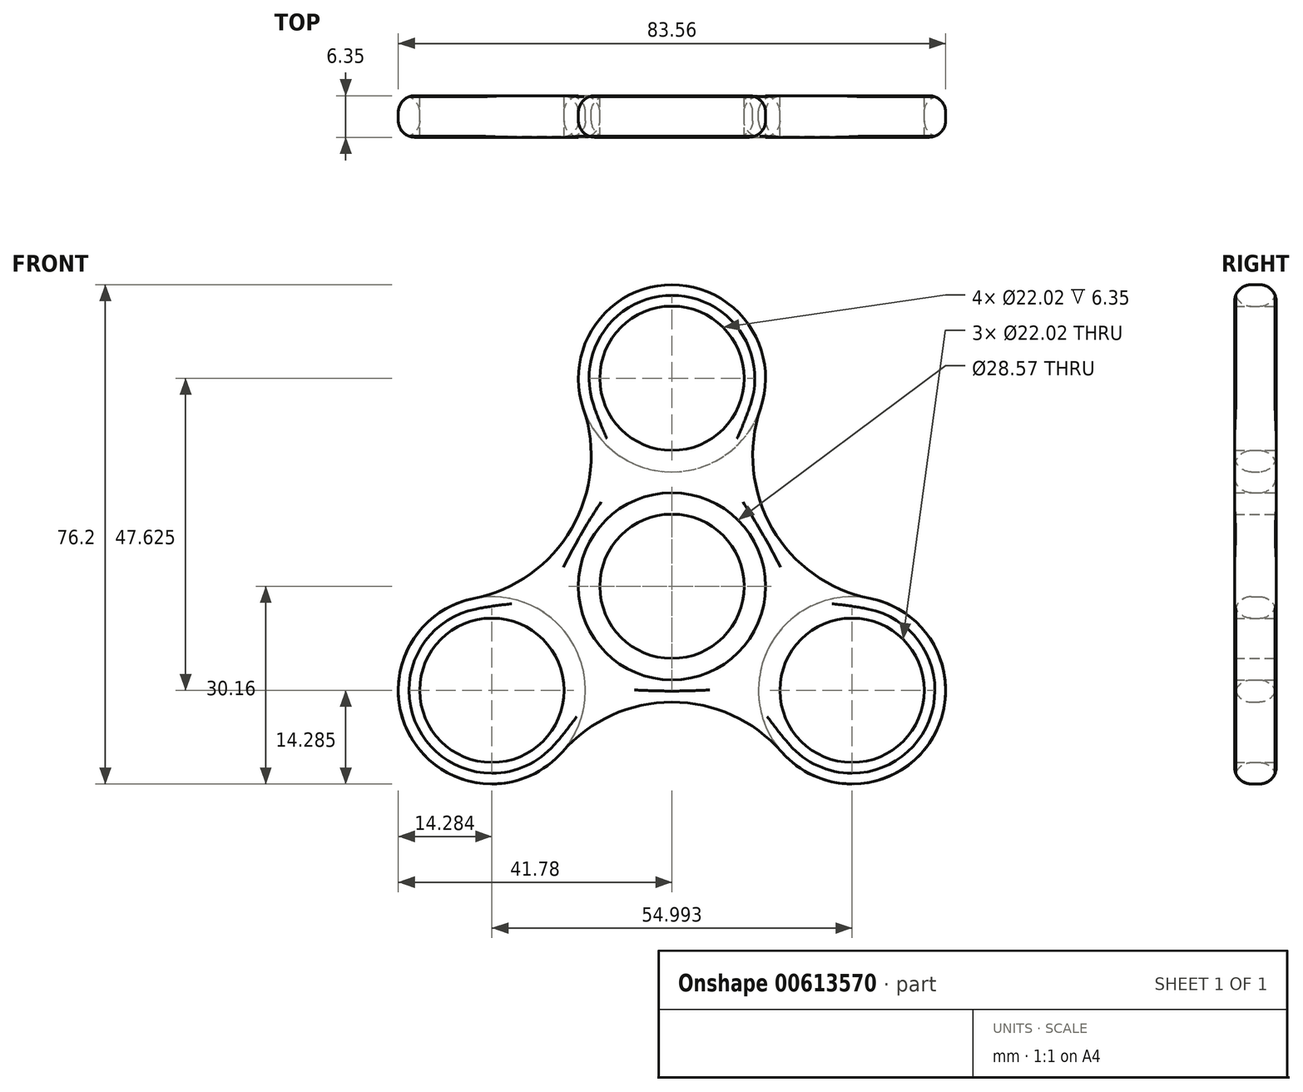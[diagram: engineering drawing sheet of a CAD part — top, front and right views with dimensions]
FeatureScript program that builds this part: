
annotation { "Feature Type Name" : "Feature", "Feature Type Description" : "" }
export const myFeature = defineFeature(function(context is Context, id is Id, definition is map)
    precondition{}
    {
        {
            var Q0;
            Q0=qCreatedBy(makeId("Front.planeOp"),FACE);
            var sketch = newSketch(context, id + "F0", { "sketchPlane" : qUnion([Q0])});
            skCircle(sketch, "E0", {"center": v(0, 0) * mm, "radius": 14.29 * mm});
            skCircle(sketch, "E1", {"center": v(0, 0) * mm, "radius": 11.01 * mm});
            skCircle(sketch, "E2", {"center": v(0, 31.75) * mm, "radius": 14.29 * mm});
            skCircle(sketch, "E3", {"center": v(0, 31.75) * mm, "radius": 11.01 * mm});
            skCircle(sketch, "E4.1.0", {"center": v(-27.5, -15.87) * mm, "radius": 11.01 * mm});
            skCircle(sketch, "E4.1.1", {"center": v(-27.5, -15.87) * mm, "radius": 14.29 * mm});
            skCircle(sketch, "E4.2.0", {"center": v(27.5, -15.88) * mm, "radius": 11.01 * mm});
            skCircle(sketch, "E4.2.1", {"center": v(27.5, -15.88) * mm, "radius": 14.29 * mm});
            skSolve(sketch);
        }
        {
            var Q0;
            Q0=makeQuery(id+"F0.imprint","IMPRINT",FACE,{"disambiguationData":[TD([[makeQuery(id+"F0.imprint","IMPRINT",EDGE,{"derivedFrom":sQuery(id+"F0.wireOp",EDGE,"E3")}),1.0]])]});
            var sketch = newSketch(context, id + "F1", { "sketchPlane" : qUnion([Q0])});
            skCircle(sketch, "E5.0", {"center": v(0, 31.75) * mm, "radius": 14.29 * mm});
            skCircle(sketch, "E6.0", {"center": v(-27.5, -15.87) * mm, "radius": 14.29 * mm});
            skCircle(sketch, "E7.0", {"center": v(0, 0) * mm, "radius": 14.29 * mm});
            skCircle(sketch, "E8.0", {"center": v(27.5, -15.88) * mm, "radius": 14.29 * mm});
            skArc(sketch, "E9", {"start": v(-30.26, -1.86) * mm, "mid": v(-15.3, 8.84) * mm, "end": v(-13.52, 27.13) * mm});
            skArc(sketch, "E10", {"start": v(13.52, 27.13) * mm, "mid": v(15.3, 8.84) * mm, "end": v(30.26, -1.86) * mm});
            skArc(sketch, "E11", {"start": v(16.74, -25.28) * mm, "mid": v(0, -17.67) * mm, "end": v(-16.74, -25.28) * mm});
            skCircle(sketch, "E12", {"center": v(0, 0) * mm, "radius": 11.01 * mm});
            skCircle(sketch, "E13", {"center": v(27.5, -15.88) * mm, "radius": 11.01 * mm});
            skCircle(sketch, "E14", {"center": v(-27.5, -15.87) * mm, "radius": 11.01 * mm});
            skCircle(sketch, "E15", {"center": v(0, 31.75) * mm, "radius": 11.01 * mm});
            skSolve(sketch);
        }
        {
            var Q0;
            Q0=makeQuery(id+"F0.imprint","IMPRINT",FACE,{"disambiguationData":[TD([[makeQuery(id+"F0.imprint","IMPRINT",EDGE,{"derivedFrom":sQuery(id+"F0.wireOp",EDGE,"E2")}),1.0]])]});
            var Q1;
            Q1=makeQuery(id+"F0.imprint","IMPRINT",FACE,{"disambiguationData":[TD([[makeQuery(id+"F0.imprint","IMPRINT",EDGE,{"derivedFrom":sQuery(id+"F0.wireOp",EDGE,"E0")}),1.0]])]});
            var Q2;
            Q2 = qSketchRegion(id + "F1", true);
            var Q3;
            Q3=makeQuery(id+"F0.imprint","IMPRINT",FACE,{"disambiguationData":[TD([[makeQuery(id+"F0.imprint","IMPRINT",EDGE,{"derivedFrom":sQuery(id+"F0.wireOp",EDGE,"E4.1.0")}),-1.0]])]});
            var Q4;
            Q4=makeQuery(id+"F0.imprint","IMPRINT",FACE,{"disambiguationData":[TD([[makeQuery(id+"F0.imprint","IMPRINT",EDGE,{"derivedFrom":sQuery(id+"F0.wireOp",EDGE,"E4.2.0")}),-1.0]])]});
            extrude(context, id + "F2", {"entities" : qUnion([Q0, Q1, Q2, Q3, Q4]), "depth" : 6.35 * mm, "offsetDistance" : 25.4 * mm});
        }
        {
            var Q0;
            Q0=makeQuery(id+"F2.opExtrude","CAP_FACE",FACE,{"disambiguationData":[OSD([sQuery(id+"F1.wireOp",EDGE,"E5.0"),sQuery(id+"F1.wireOp",EDGE,"E6.0"),sQuery(id+"F1.wireOp",EDGE,"E7.0"),sQuery(id+"F1.wireOp",EDGE,"E8.0"),sQuery(id+"F1.wireOp",EDGE,"E9"),sQuery(id+"F1.wireOp",EDGE,"E10"),sQuery(id+"F1.wireOp",EDGE,"E11"),sQuery(id+"F1.wireOp",EDGE,"E13"),sQuery(id+"F1.wireOp",EDGE,"E14"),sQuery(id+"F1.wireOp",EDGE,"E15")])],"isStart":false});
            var Q1;
            Q1=makeQuery(id+"F2.opExtrude","CAP_FACE",FACE,{"disambiguationData":[OSD([sQuery(id+"F1.wireOp",EDGE,"E5.0"),sQuery(id+"F1.wireOp",EDGE,"E6.0"),sQuery(id+"F1.wireOp",EDGE,"E7.0"),sQuery(id+"F1.wireOp",EDGE,"E8.0"),sQuery(id+"F1.wireOp",EDGE,"E9"),sQuery(id+"F1.wireOp",EDGE,"E10"),sQuery(id+"F1.wireOp",EDGE,"E11"),sQuery(id+"F1.wireOp",EDGE,"E13"),sQuery(id+"F1.wireOp",EDGE,"E14"),sQuery(id+"F1.wireOp",EDGE,"E15")])],"isStart":true});
            fillet(context, id + "F3", {"entities" : qUnion([Q0, Q1]), "radius" : 2.54 * mm, "tangentPropagation" : true, "allowEdgeOverflow" : false});
        }
        {
            var Q0;
            Q0=makeQuery(id+"F2.opExtrude","CAP_EDGE",EDGE,{"disambiguationData":[OSD([sQuery(id+"F0.wireOp",EDGE,"E2")])],"isStart":false});
            var Q1;
            Q1=makeQuery(id+"F2.opExtrude","CAP_EDGE",EDGE,{"disambiguationData":[OSD([sQuery(id+"F0.wireOp",EDGE,"E4.1.1")])],"isStart":false});
            var Q2;
            Q2=makeQuery(id+"F2.opExtrude","CAP_EDGE",EDGE,{"disambiguationData":[OSD([sQuery(id+"F0.wireOp",EDGE,"E4.2.1")])],"isStart":false});
            var Q3;
            Q3=makeQuery(id+"F2.opExtrude","CAP_EDGE",EDGE,{"disambiguationData":[OSD([sQuery(id+"F0.wireOp",EDGE,"E2")])],"isStart":true});
            var Q4;
            Q4=makeQuery(id+"F2.opExtrude","CAP_EDGE",EDGE,{"disambiguationData":[OSD([sQuery(id+"F0.wireOp",EDGE,"E4.1.1")])],"isStart":true});
            var Q5;
            Q5=makeQuery(id+"F2.opExtrude","CAP_EDGE",EDGE,{"disambiguationData":[OSD([sQuery(id+"F0.wireOp",EDGE,"E4.2.1")])],"isStart":true});
            fillet(context, id + "F4", {"entities" : qUnion([Q0, Q1, Q2, Q3, Q4, Q5]), "radius" : 2.54 * mm, "tangentPropagation" : true, "allowEdgeOverflow" : false});
        }
    });
